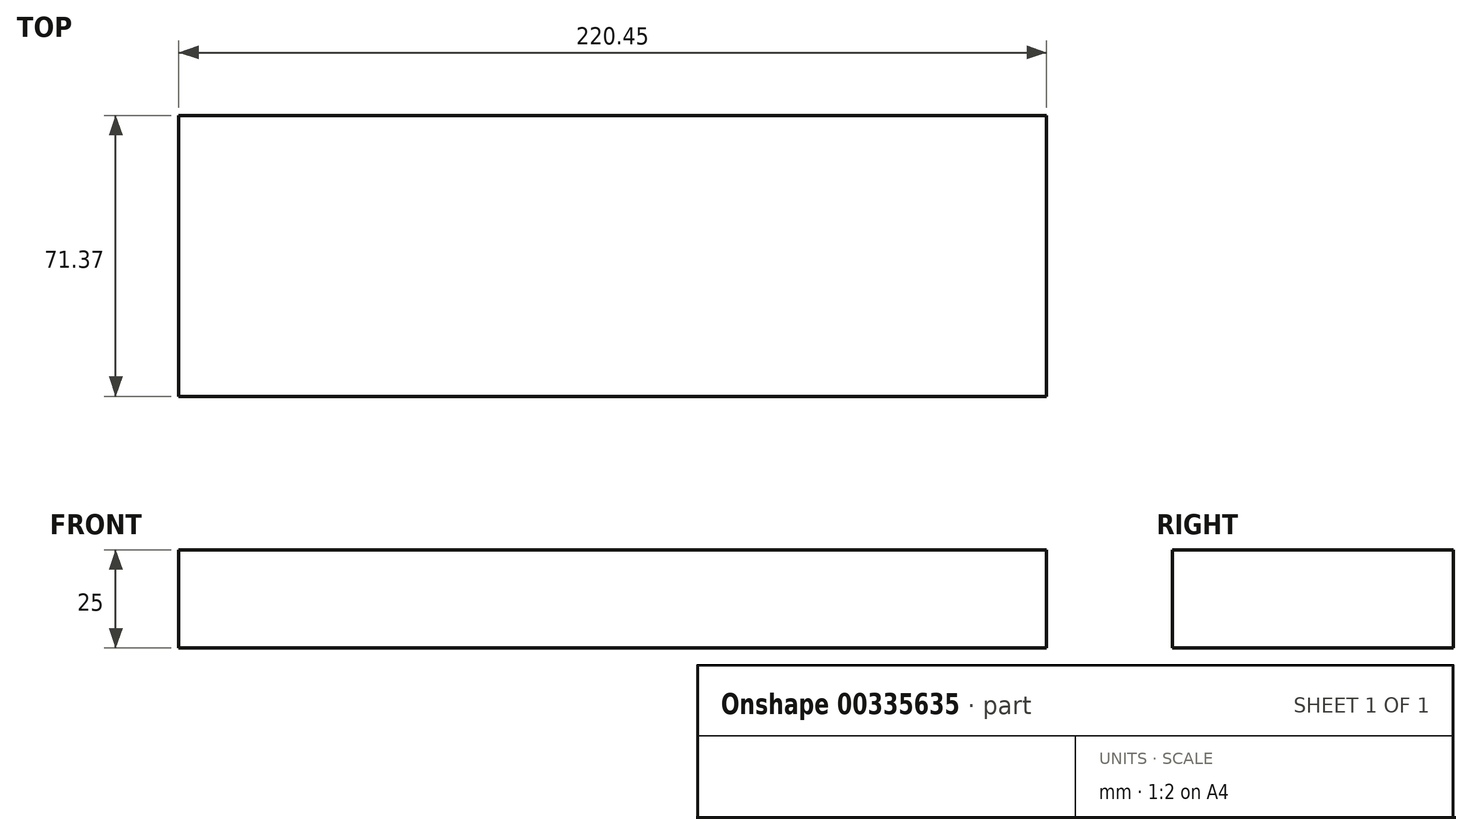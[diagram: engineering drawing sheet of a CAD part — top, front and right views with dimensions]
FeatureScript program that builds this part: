
annotation { "Feature Type Name" : "Feature", "Feature Type Description" : "" }
export const myFeature = defineFeature(function(context is Context, id is Id, definition is map)
    precondition{}
    {
        {
            var Q0;
            Q0=qCreatedBy(makeId("Top.planeOp"),FACE);
            var sketch = newSketch(context, id + "F0", { "sketchPlane" : qUnion([Q0])});
            skLineSegment(sketch, "E0.bottom", {"start": v(-97.27, 43.98) * mm, "end": v(123.18, 43.98) * mm});
            skLineSegment(sketch, "E0.top", {"start": v(-97.27, -27.39) * mm, "end": v(123.18, -27.39) * mm});
            skLineSegment(sketch, "E0.left", {"start": v(-97.27, 43.98) * mm, "end": v(-97.27, -27.39) * mm});
            skLineSegment(sketch, "E0.right", {"start": v(123.18, 43.98) * mm, "end": v(123.18, -27.39) * mm});
            skSolve(sketch);
        }
        {
            var Q0;
            Q0 = qSketchRegion(id + "F0", true);
            extrude(context, id + "F1", {"entities" : qUnion([Q0]), "depth" : 25 * mm});
        }
    });
